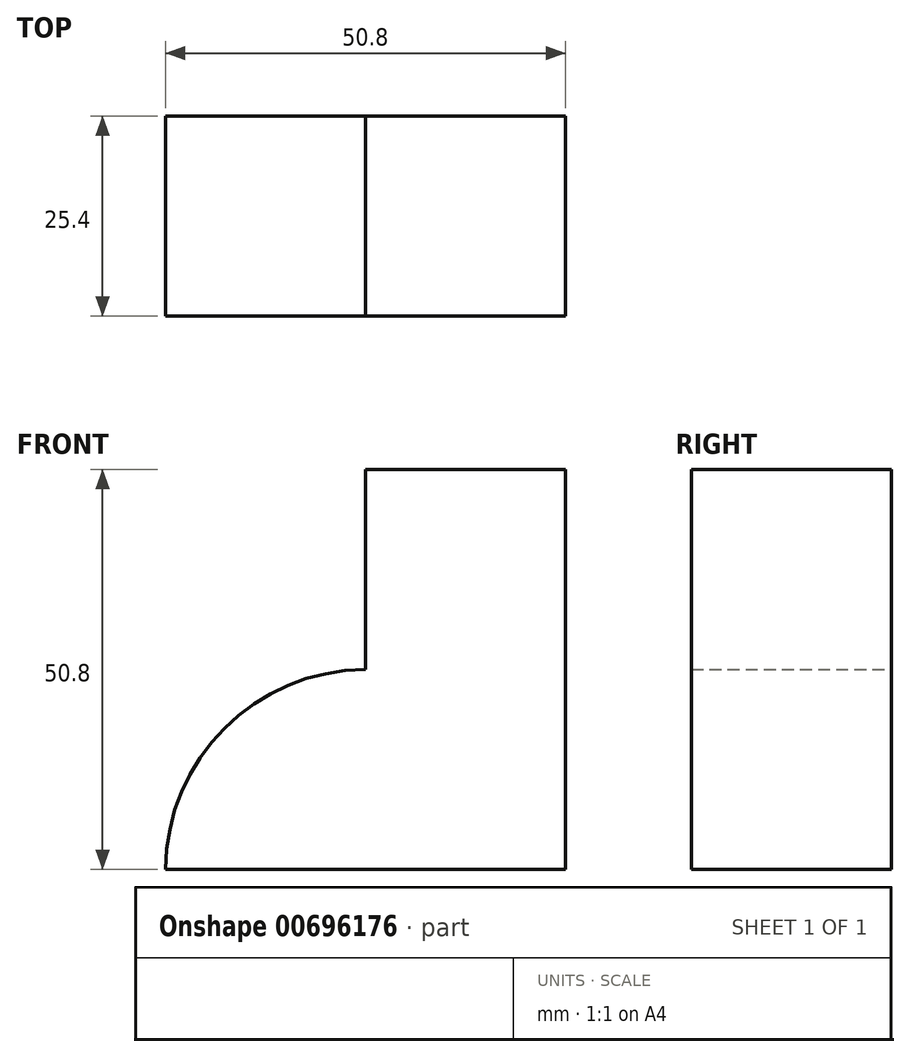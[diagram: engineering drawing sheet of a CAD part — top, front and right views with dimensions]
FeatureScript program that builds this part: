
annotation { "Feature Type Name" : "Feature", "Feature Type Description" : "" }
export const myFeature = defineFeature(function(context is Context, id is Id, definition is map)
    precondition{}
    {
        {
            var Q0;
            Q0=qCreatedBy(makeId("Front.planeOp"),FACE);
            var sketch = newSketch(context, id + "F0", { "sketchPlane" : qUnion([Q0])});
            skLineSegment(sketch, "E0", {"start": v(34.28, 50.8) * mm, "end": v(34.28, 0) * mm});
            skLineSegment(sketch, "E1", {"start": v(34.28, 0) * mm, "end": v(-16.52, 0) * mm});
            skLineSegment(sketch, "E2", {"start": v(34.28, 50.8) * mm, "end": v(8.88, 50.8) * mm});
            skLineSegment(sketch, "E3", {"start": v(8.88, 50.8) * mm, "end": v(8.88, 25.4) * mm});
            skArc(sketch, "E4", {"start": v(8.88, 25.4) * mm, "mid": v(-9.04, 17.93) * mm, "end": v(-16.52, 0) * mm});
            skSolve(sketch);
        }
        {
            var Q0;
            Q0=makeQuery(id+"F0.imprint","IMPRINT",FACE,{"disambiguationData":[TD([[makeQuery(id+"F0.imprint","IMPRINT",EDGE,{"derivedFrom":sQuery(id+"F0.wireOp",EDGE,"E0")}),-1.0]])]});
            extrude(context, id + "F1", {"entities" : qUnion([Q0]), "depth" : 25.4 * mm, "offsetDistance" : 25.4 * mm});
        }
    });
